# Revit family: rinnai_linear0800_ss
name_source: partatom
category: Specialty Equipment
units: mm (PartAtom-declared; Revit-internal decimal feet)

## family parameters
Always vertical = Yes
Cut with Voids When Loaded = Yes
Host = Wall
Part Type = Normal
Room Calculation Point = No
Round Connector Dimension = Use Diameter
Shared = No

## types (1)
- rinnai_linear0800_ss
    Description = Linear 800 Single sided Fireplace
    Double Sided = No
    Fire Window Wall Cut = 5 mm  [stored 0.0164042 ft]
    Front Offset to middle to middle of fire = 212 mm  [stored 0.695538 ft]
    Manufacturer = Rinnai NZ Ltd
    Model = Linear 0800 Single Sided
    Type Comments = Linear 800 Single Sided
    URL = www.rinnai.co.nz
    _fire_centre_depth = 285 mm  [stored 0.935039 ft]
    _fire_clearceiling = 1000 mm  [stored 3.28084 ft]
    _fire_cleardepth = 1000 mm  [stored 3.28084 ft]
    _fire_clearheight = 400 mm  [stored 1.31234 ft]
    _fire_side_clearance = 400 mm  [stored 1.31234 ft]
    _fire_top = 969 mm
    _fire_width = 1150 mm
    _fire_window_top = 536 mm
    _fire_window_width = 830 mm  [stored 2.7231 ft]
    _opening_depth = 570 mm  [stored 1.87008 ft]
    _opening_height = 1019 mm
    _opening_width = 1250 mm  [stored 4.10105 ft]
    clearance = 50 mm  [stored 0.164042 ft]
    m_body = Rinnai Body
    m_cowl = Rinnai Cowl
    m_firebox = Rinnai_firebox
    m_flames = Rinnai Flames
    m_flue = Rinnai Flue
    m_frame = Rinnai Black Frame
    m_gas = Rinnai Gas
    m_glass = Rinnai_fireglass
    m_plinth = <By Category>
    m_rinnai = Rinnai_logo
    opening floor offset = 0 mm  [stored 0 ft]
    v_back = Yes
    v_fireplace = Yes

note: [stored X ft] marks values corroborated as IEEE doubles in the binary element streams (Revit-internal decimal feet)

## geometry (parser evidence)
native form markers: Sweep x57
no freeform markers — native parametric forms only
